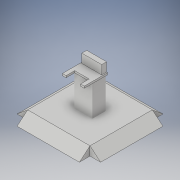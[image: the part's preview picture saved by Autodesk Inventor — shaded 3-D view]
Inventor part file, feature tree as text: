
AUTODESK INVENTOR PART (.ipt)
format: ipt  version: 2017 (Build 210142000, 142)  size: 390,656 bytes
history: native  units: in
note: dims shown in document units (in); Inventor stores cm internally (conversion verified against a paired STEP export)
features: other x8, extrude x8, sketch x7, pattern_circular x1, plane x1, loft x1
ambient origin geometry x7: Origin, YZ Plane, XY Plane, X Axis, Y Axis, Z Axis, Center Point
bodies: Solid4 (feature_tree)
feature tree (26):
  other  "bace + terminal"
  extrude  "Extrusion16"  Depth=1.0in
  extrude  "arm rests and terminal monitor"  Depth=0.85in
  other  "middle of the part vertical"
  other  "used to line up the key board and mouse"
  extrude  "bace"  Depth=0.75in
  extrude  "ramp to terminal"  Depth=1.0in
  pattern_circular  "made rest of ramps to terminal"  [2 undecoded]
  other  "mate to back to monitor"
  extrude  "monitor raise"  Depth=0.0181in
  sketch  "Sketch26"  dims[d27=1.1in d28=0.75in]
  plane  "Work Plane20"
  loft  "outlet cap"
  sketch  "Sketch28"  dims[d29=1.0in d30=0.65in]
  extrude  "outlet revele out"  Depth=0.2083in TaperAngle=0.0deg
  extrude  "hot and ground wire holes"  Depth=1.125in
  other  "screw workplane"
  other  "screw made"
  extrude  "slot for screw"  Depth=0.0181in
  other  "bottom workplane"
  other  "bace of terminal"
  sketch  "Sketch23"  dims[d0=1.0in d1=0.75in]
  sketch  "Sketch25"  dims[d19=1.2in d20=0.85in]
  sketch  "Sketch29"  dims[d42=1.1in d43=0.85in d44=1.0in d45=0.75in d49=1.2in d50=0.85in d51=1.0in d52=0.75in]
  sketch  "Sketch30"  dims[d123=1.0in d124=0.0in]
  sketch  "Sketch31"  dims[d163=0.8125in d165=0.4167in d166=0.8125in d167=0.4167in d168=0.2083in d169=0.0in d170=1.125in d173=1.8892in d175=1.125in d178=1.0in d179=0.0in d182=0.2318in d183=0.3777in d185=0.05in d186=0.0678in d188=0.1962in d189=0.3421in d190=0.0in d191=90.0deg d192=0.0in d193=90.0deg d194=0.0251in d195=0.0305in d197=0.0931in d198=0.0311in d199=0.0362in d200=0.0045in d201=0.0208in d202=0.0208in d203=0.0078in d204=0.0291in d205=0.0078in d206=0.0362in d207=0.0045in d208=0.0208in d209=0.0078in d211=0.0078in d212=0.0208in d213=0.0181in d214=0.0291in d221=0.003in d222=0.0in d223=0.0649in d224=0.0in d225=90.0deg d226=0.0108in d227=0.0027in d228=90.0deg d229=0.0015in d230=0.0128in d231=0.0in d232=3.6493in d233=0.0in d234=0.1564in d235=0.2069in d236=7.0in d237=7.0in d238=0.2749in d239=3.6493in d240=0.0in d241=1.5748in d242=360.0deg d244=0.0in d245=0.5527in d246=2.2315in d247=0.1134in d248=0.0181in]
note: 2 required parameter values undecoded (feature->parameter linkage not recoverable at this tier; creation-order binding heuristic only, values carry confidence <= 0.55)
